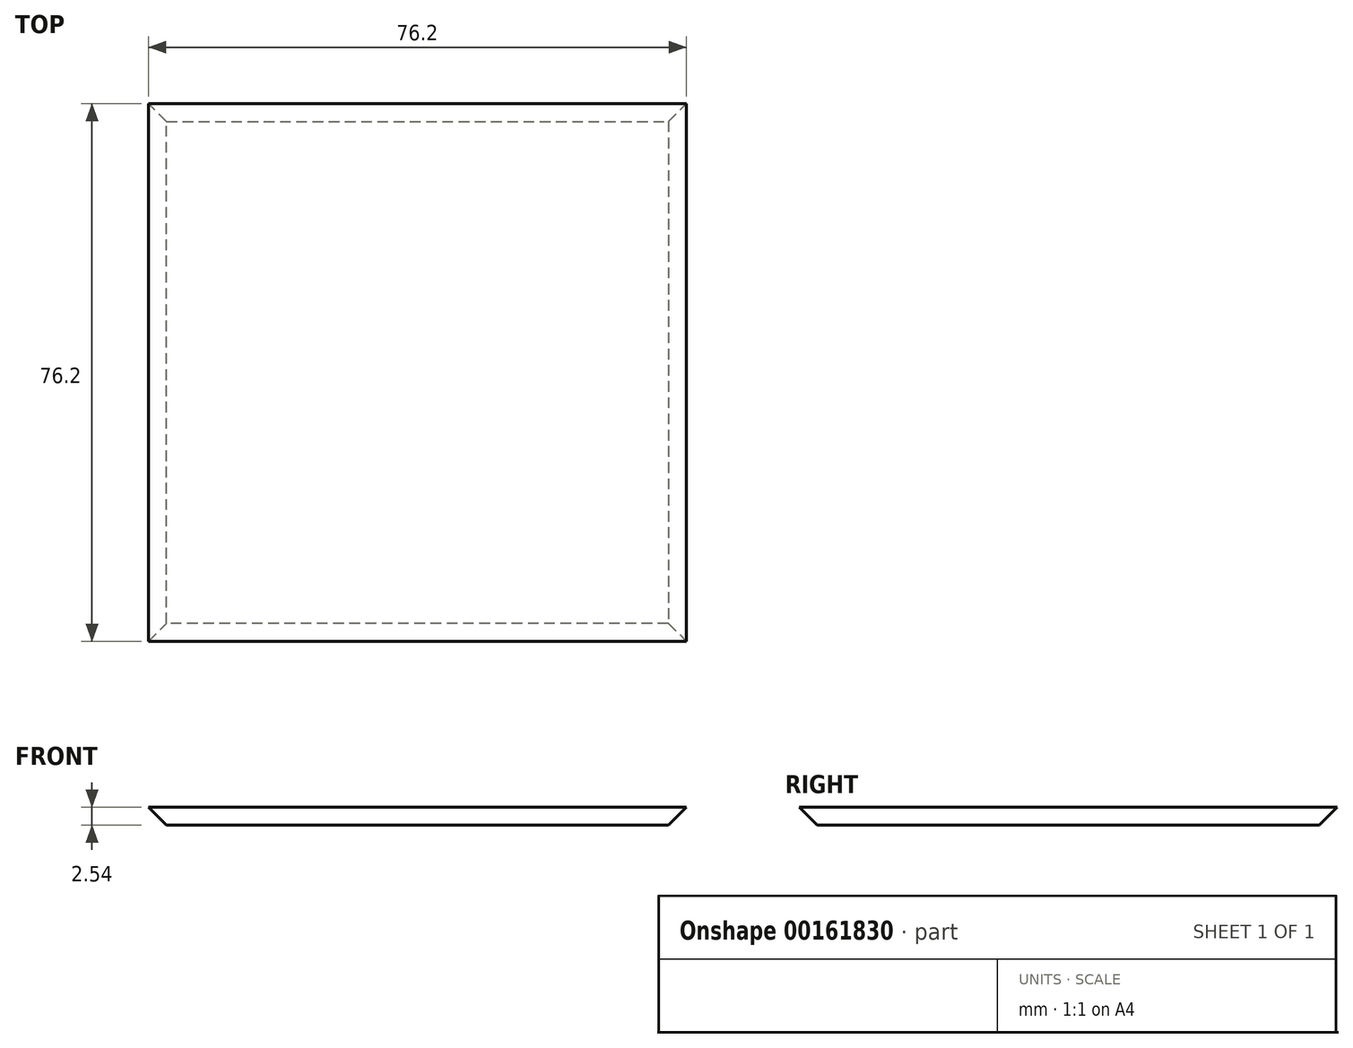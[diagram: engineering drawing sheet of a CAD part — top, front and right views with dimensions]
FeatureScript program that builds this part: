
annotation { "Feature Type Name" : "Feature", "Feature Type Description" : "" }
export const myFeature = defineFeature(function(context is Context, id is Id, definition is map)
    precondition{}
    {
        {
            var Q0;
            Q0=qCreatedBy(makeId("Top.planeOp"),FACE);
            var sketch = newSketch(context, id + "F0", { "sketchPlane" : qUnion([Q0])});
            skLineSegment(sketch, "E0.bottom", {"start": v(0, 0) * mm, "end": v(76.2, 0) * mm});
            skLineSegment(sketch, "E0.top", {"start": v(0, 76.2) * mm, "end": v(76.2, 76.2) * mm});
            skLineSegment(sketch, "E0.left", {"start": v(0, 0) * mm, "end": v(0, 76.2) * mm});
            skLineSegment(sketch, "E0.right", {"start": v(76.2, 0) * mm, "end": v(76.2, 76.2) * mm});
            skSolve(sketch);
        }
        {
            var Q0;
            Q0 = qSketchRegion(id + "F0", true);
            extrude(context, id + "F1", {"entities" : qUnion([Q0]), "depth" : 2.54 * mm});
        }
        {
            var Q0;
            Q0=makeQuery(id+"F1.opExtrude","CAP_FACE",FACE,{"disambiguationData":[OSD([sQuery(id+"F0.wireOp",EDGE,"E0.bottom"),sQuery(id+"F0.wireOp",EDGE,"E0.top"),sQuery(id+"F0.wireOp",EDGE,"E0.left"),sQuery(id+"F0.wireOp",EDGE,"E0.right")])],"isStart":true});
            chamfer(context, id + "F2", {"entities" : qUnion([Q0]), "width" : 2.54 * mm, "tangentPropagation" : true});
        }
    });
